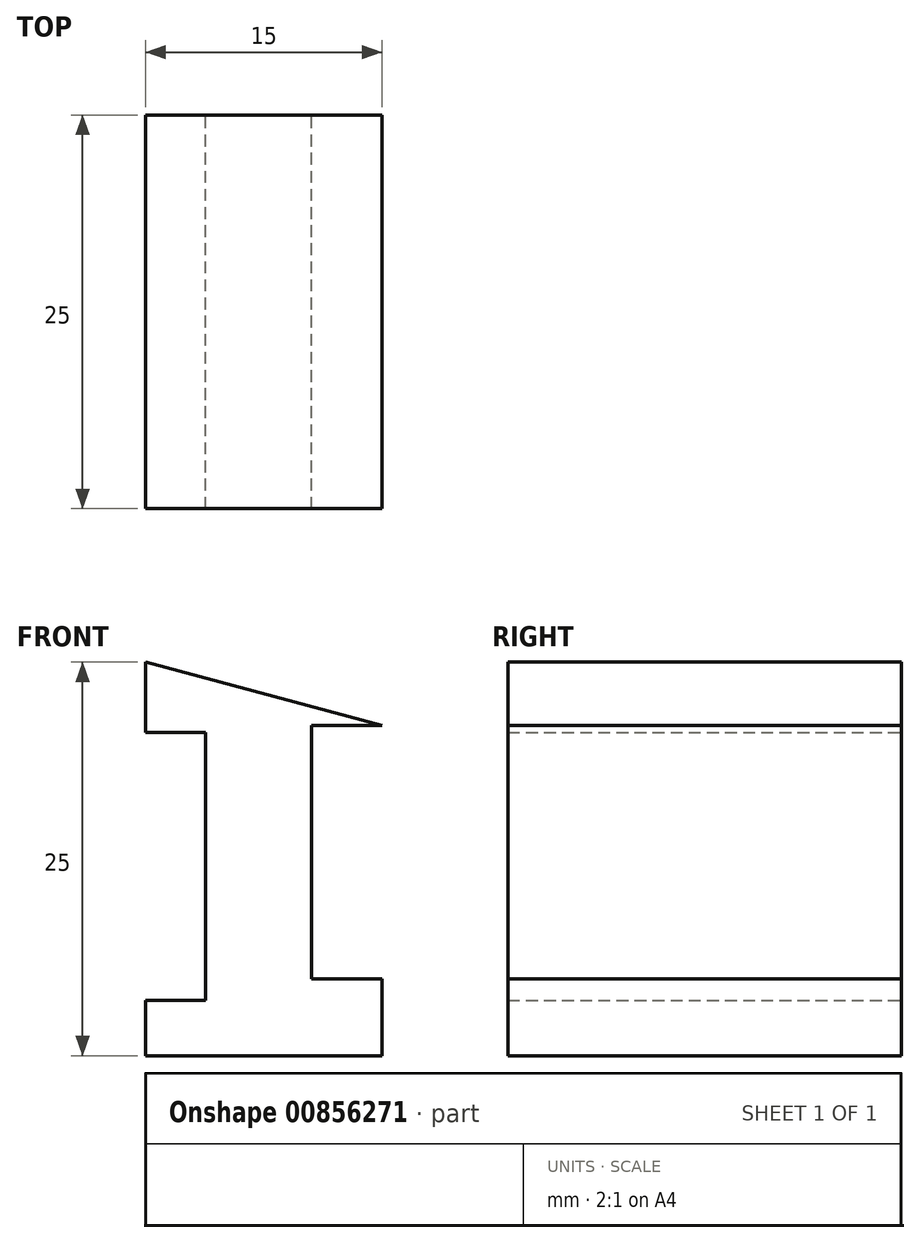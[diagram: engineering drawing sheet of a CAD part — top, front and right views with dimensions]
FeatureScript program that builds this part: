
annotation { "Feature Type Name" : "Feature", "Feature Type Description" : "" }
export const myFeature = defineFeature(function(context is Context, id is Id, definition is map)
    precondition{}
    {
        {
            var Q0;
            Q0=qCreatedBy(makeId("Front.planeOp"),FACE);
            var sketch = newSketch(context, id + "F0", { "sketchPlane" : qUnion([Q0])});
            skLineSegment(sketch, "E0.bottom", {"start": v(-8.4, 13.98) * mm, "end": v(6.6, 13.98) * mm});
            skLineSegment(sketch, "E0.top", {"start": v(-8.4, -11.02) * mm, "end": v(6.6, -11.02) * mm});
            skLineSegment(sketch, "E0.left", {"start": v(-8.4, 13.98) * mm, "end": v(-8.4, -11.02) * mm});
            skLineSegment(sketch, "E0.right", {"start": v(6.6, 13.98) * mm, "end": v(6.6, -11.02) * mm});
            skLineSegment(sketch, "E1.bottom", {"start": v(6.6, 9.96) * mm, "end": v(2.13, 9.96) * mm});
            skLineSegment(sketch, "E1.top", {"start": v(6.6, -6.15) * mm, "end": v(2.13, -6.15) * mm});
            skLineSegment(sketch, "E1.left", {"start": v(6.6, 9.96) * mm, "end": v(6.6, -6.15) * mm});
            skLineSegment(sketch, "E1.right", {"start": v(2.13, 9.96) * mm, "end": v(2.13, -6.15) * mm});
            skLineSegment(sketch, "E2.bottom", {"start": v(-8.4, 9.5) * mm, "end": v(-4.59, 9.5) * mm});
            skLineSegment(sketch, "E2.top", {"start": v(-8.4, -7.5) * mm, "end": v(-4.59, -7.5) * mm});
            skLineSegment(sketch, "E2.left", {"start": v(-8.4, 9.5) * mm, "end": v(-8.4, -7.5) * mm});
            skLineSegment(sketch, "E2.right", {"start": v(-4.59, 9.5) * mm, "end": v(-4.59, -7.5) * mm});
            skLineSegment(sketch, "E3", {"start": v(-8.4, 13.98) * mm, "end": v(6.6, 9.96) * mm});
            skLineSegment(sketch, "E4", {"start": v(6.6, 9.96) * mm, "end": v(6.6, 13.98) * mm});
            skSolve(sketch);
        }
        {
            var Q0;
            Q0 = qSketchRegion(id + "F0", true);
            extrude(context, id + "F1", {"entities" : qUnion([Q0]), "depth" : 25 * mm, "offsetDistance" : 25 * mm});
        }
        {
            var Q0;
            Q0=makeQuery(id+"F0.imprint","IMPRINT",FACE,{"disambiguationData":[TD([[makeQuery(id+"F0.imprint","IMPRINT",EDGE,{"derivedFrom":sQuery(id+"F0.wireOp",EDGE,"E1.bottom")}),1.0]])]});
            var Q1;
            Q1=makeQuery(id+"F0.imprint","IMPRINT",FACE,{"disambiguationData":[TD([[makeQuery(id+"F0.imprint","IMPRINT",EDGE,{"derivedFrom":sQuery(id+"F0.wireOp",EDGE,"E2.bottom")}),-1.0]])]});
            extrude(context, id + "F2", {"entities" : qUnion([Q0, Q1]), "operationType" : NewBodyOperationType.REMOVE, "endBound" : BoundingType.THROUGH_ALL, "depth" : 1 * mm, "offsetDistance" : 25 * mm});
        }
        {
            var Q0;
            Q0=makeQuery(id+"F0.imprint","IMPRINT",FACE,{"disambiguationData":[TD([[makeQuery(id+"F0.imprint","IMPRINT",EDGE,{"derivedFrom":sQuery(id+"F0.wireOp",EDGE,"E3")}),1.0]])]});
            extrude(context, id + "F3", {"entities" : qUnion([Q0]), "operationType" : NewBodyOperationType.REMOVE, "depth" : 46 * mm, "offsetDistance" : 25 * mm});
        }
    });
